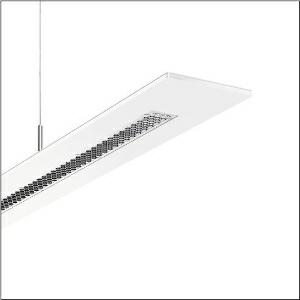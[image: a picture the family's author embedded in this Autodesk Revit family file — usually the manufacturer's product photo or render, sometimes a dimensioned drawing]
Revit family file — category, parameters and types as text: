
# Revit family: arktika_r__21_5mb251dl30840_e160
name_source: partatom
category: Lighting Fixtures
units: mm (PartAtom-declared; Revit-internal decimal feet)

## family parameters
Cut with Voids When Loaded = No
Host = Face
Light Source = No
Part Type = Normal
Room Calculation Point = No
Round Connector Dimension = Use Diameter
Shared = No

## types (1)
- --- (1 x LED 4000K / CRI = 80 (unbekannt), 4400 lm, 4000K)
    Apparent Load = 34 VA
    CIE Flux Codes = 81 100 100 79 100
    Color Rendering = 80
    Color Temperature = 4000K
    Default Elevation = 1800 mm
    Description = Arktika® 21, office luminaire, primary anti-glare with honeycomb louvre, of plastic, aluminium vaporised, highly specular, light emission: direct/indirect distribution, primary light characteristic: symmetric, installation type: suspended mounting, LED, rated luminous flux: 4.400lm, luminous efficacy: 131lm/W, light colour: 840, colour temperature: 4000K, control gear: DALI, with terminal, 3+2-pole, max. 2.5mm², mains connection: 220..240V, AC, 50/60Hz, rated input power: 34W, housing, of aluminium, powder-coated, traffic white (RAL 9016), 1-length, length: 1.250mm, width: 120mm, height: 8mm, protection rating (complete): IP20, insulation class (complete): insulation class II (safety insulation), certification: CE, ENEC, VDE, packaging unit: 1 piece
    Height = 8 mm  [stored 0.0262467 ft]
    Lamp = 1 x LED 4000K / CRI >= 80 (unbekannt)
    Lamp Light Flux = 4400 lm
    Lamp count = 1
    Length = 1250 mm
    Luminous efficacy = 131 lm/W
    Manufacturer = Siteco
    ModVariant = No
    Model = 5MB251DL30840
    Mounting Place = Ceiling
    Mounting Type = Pendant
    Number of Poles = 1
    OnlyDefault = Yes
    Power Factor = 1
    Product Name = Arktika® 21
    Product group = office luminaire | ceiling pendant
    ProductGroupID = 904
    Protection Class = Protection class II
    Protection Degree = IP 20
    RLX_Detail_Level = 1
    RLX_Emergency_Light_Flux = 0 lm
    RLX_Emergency_Type = 0
    RLX_Emergency_Type_DB = No
    RlxData = <blob elided: 39225 chars, md5=58960cb6>
    Socket = socket
    Standby Power = 0 W
    System Light Flux = 4400 lm
    System Power = 34 W
    Type Comments = factory setting: luminous flux: 100 % | dim-lin: 254 | 665 mA
    Type Image = l_1006128.jpg
    URL = http://relux.com
    VarID = @adj_202956
    Voltage = 0 V
    Weight = 0.00 kg
    Width = 120 mm

note: [stored X ft] marks values corroborated as IEEE doubles in the binary element streams (Revit-internal decimal feet)

## geometry (parser evidence)
native form markers: Blend x4, Sweep x11
no freeform markers — native parametric forms only
